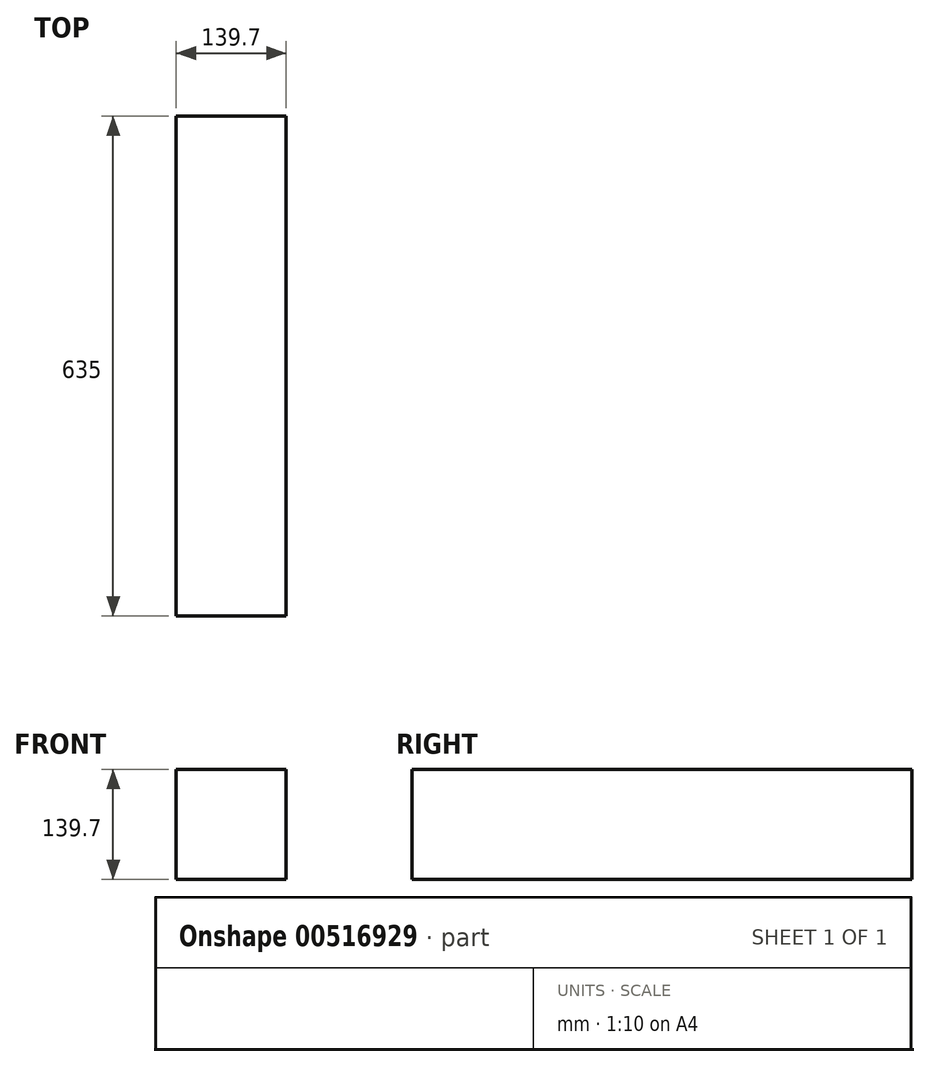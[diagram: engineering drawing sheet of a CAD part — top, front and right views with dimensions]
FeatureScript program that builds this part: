
annotation { "Feature Type Name" : "Feature", "Feature Type Description" : "" }
export const myFeature = defineFeature(function(context is Context, id is Id, definition is map)
    precondition{}
    {
        {
            var Q0;
            Q0=qCreatedBy(makeId("Front.planeOp"),FACE);
            var sketch = newSketch(context, id + "F0", { "sketchPlane" : qUnion([Q0])});
            skLineSegment(sketch, "E0.bottom", {"start": v(0, 0) * mm, "end": v(139.7, 0) * mm});
            skLineSegment(sketch, "E0.top", {"start": v(0, 139.7) * mm, "end": v(139.7, 139.7) * mm});
            skLineSegment(sketch, "E0.left", {"start": v(0, 0) * mm, "end": v(0, 139.7) * mm});
            skLineSegment(sketch, "E0.right", {"start": v(139.7, 0) * mm, "end": v(139.7, 139.7) * mm});
            skSolve(sketch);
        }
        {
            var Q0;
            Q0 = qSketchRegion(id + "F0", true);
            extrude(context, id + "F1", {"entities" : qUnion([Q0]), "depth" : 635 * mm, "offsetDistance" : 25.4 * mm});
        }
    });
